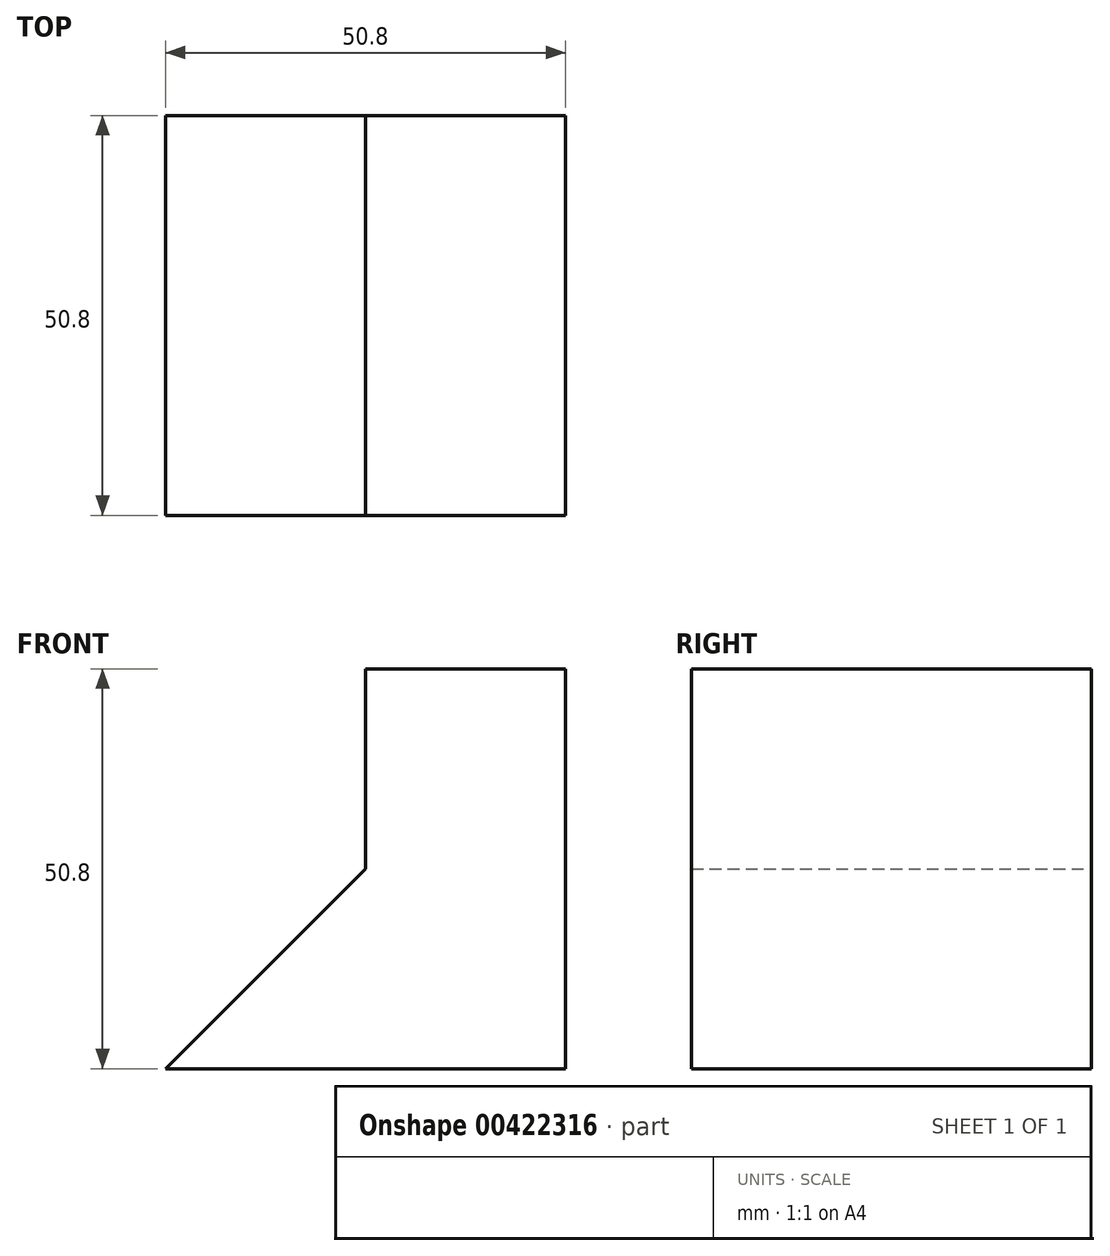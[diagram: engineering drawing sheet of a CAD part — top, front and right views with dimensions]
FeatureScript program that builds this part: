
annotation { "Feature Type Name" : "Feature", "Feature Type Description" : "" }
export const myFeature = defineFeature(function(context is Context, id is Id, definition is map)
    precondition{}
    {
        {
            var Q0;
            Q0=qCreatedBy(makeId("Front.planeOp"),FACE);
            var sketch = newSketch(context, id + "F0", { "sketchPlane" : qUnion([Q0])});
            skLineSegment(sketch, "E0", {"start": v(0, 50.8) * mm, "end": v(-25.4, 50.8) * mm});
            skLineSegment(sketch, "E1", {"start": v(-25.4, 50.8) * mm, "end": v(-25.4, 25.4) * mm});
            skLineSegment(sketch, "E2", {"start": v(0, 50.8) * mm, "end": v(0, 0) * mm});
            skLineSegment(sketch, "E3", {"start": v(0, 0) * mm, "end": v(-50.8, 0) * mm});
            skLineSegment(sketch, "E4", {"start": v(-25.4, 25.4) * mm, "end": v(-50.8, 0) * mm});
            skSolve(sketch);
        }
        {
            var Q0;
            Q0=makeQuery(id+"F0.imprint","IMPRINT",FACE,{"disambiguationData":[TD([[makeQuery(id+"F0.imprint","IMPRINT",EDGE,{"derivedFrom":sQuery(id+"F0.wireOp",EDGE,"E0")}),1.0]])]});
            extrude(context, id + "F1", {"entities" : qUnion([Q0]), "depth" : 50.8 * mm});
        }
    });
